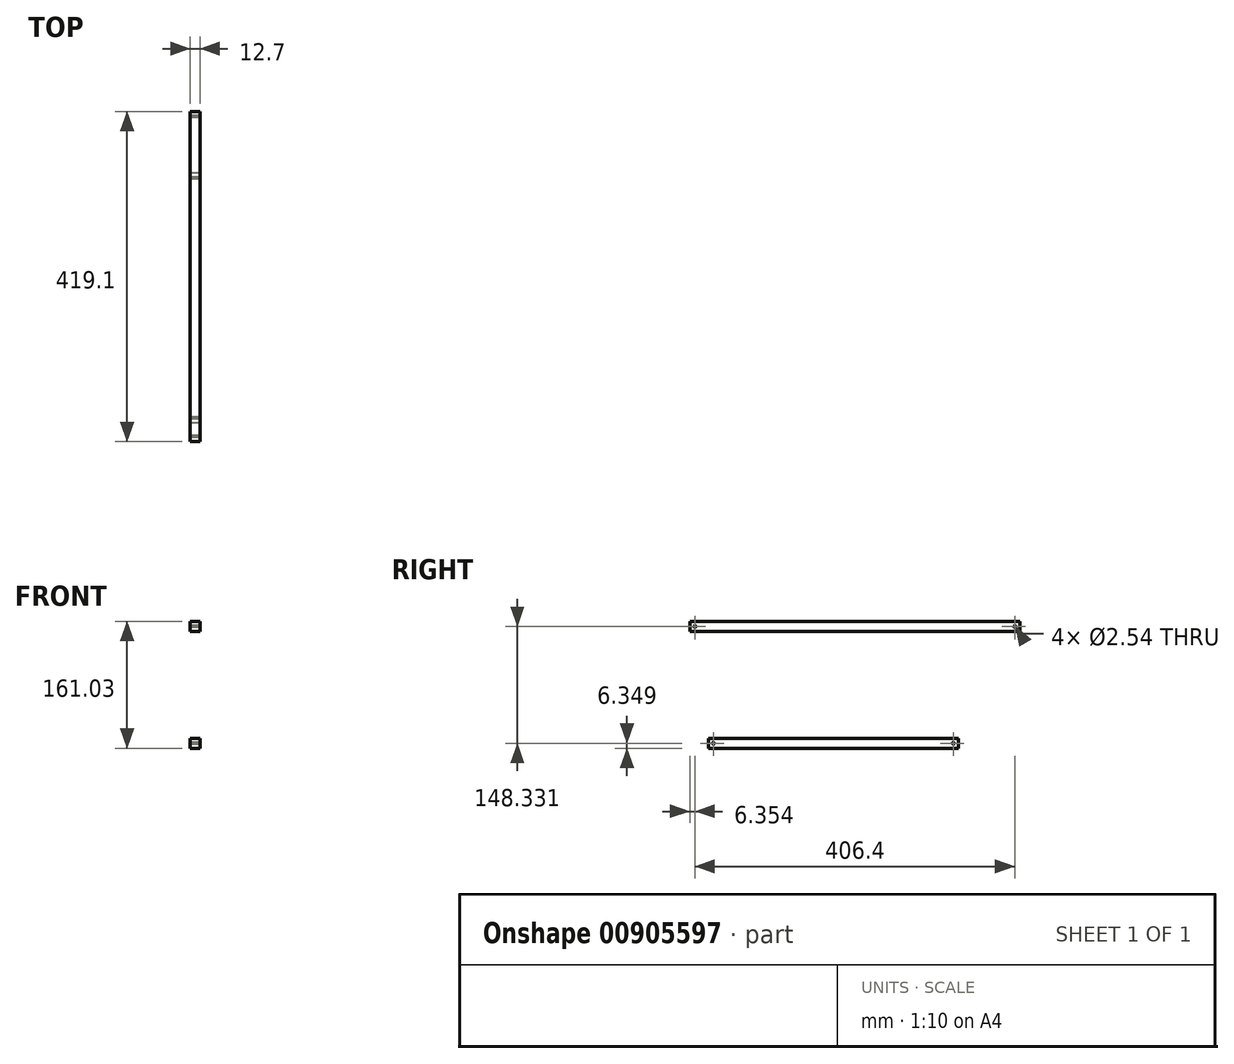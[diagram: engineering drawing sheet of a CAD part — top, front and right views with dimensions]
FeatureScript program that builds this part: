
annotation { "Feature Type Name" : "Feature", "Feature Type Description" : "" }
export const myFeature = defineFeature(function(context is Context, id is Id, definition is map)
    precondition{}
    {
        {
            var Q0;
            Q0=qCreatedBy(makeId("Right.planeOp"),FACE);
            var sketch = newSketch(context, id + "F0", { "sketchPlane" : qUnion([Q0])});
            skLineSegment(sketch, "E0", {"start": v(-773.49, 155.27) * mm, "end": v(-354.39, 155.27) * mm});
            skLineSegment(sketch, "E1", {"start": v(-773.49, 155.27) * mm, "end": v(-773.49, 142.57) * mm});
            skLineSegment(sketch, "E2", {"start": v(-773.49, 142.57) * mm, "end": v(-354.39, 142.57) * mm});
            skLineSegment(sketch, "E3", {"start": v(-354.39, 142.57) * mm, "end": v(-354.39, 155.27) * mm});
            skLineSegment(sketch, "E4", {"start": v(-750.08, 6.94) * mm, "end": v(-432.58, 6.94) * mm});
            skLineSegment(sketch, "E5", {"start": v(-432.58, 6.94) * mm, "end": v(-432.58, -5.76) * mm});
            skLineSegment(sketch, "E6", {"start": v(-432.58, -5.76) * mm, "end": v(-750.08, -5.76) * mm});
            skLineSegment(sketch, "E7", {"start": v(-750.08, -5.76) * mm, "end": v(-750.08, 6.94) * mm});
            skPoint(sketch, "E8", {"position": v(-767.14, 148.92) * mm});
            skPoint(sketch, "E9", {"position": v(-360.74, 148.92) * mm});
            skLineSegment(sketch, "E10", {"start": v(-750.08, 6.94) * mm, "end": v(-737.38, 6.94) * mm});
            skLineSegment(sketch, "E11", {"start": v(-737.38, 6.94) * mm, "end": v(-737.38, -5.76) * mm});
            skLineSegment(sketch, "E12", {"start": v(-737.38, -5.76) * mm, "end": v(-750.08, 6.94) * mm});
            skLineSegment(sketch, "E13", {"start": v(-737.38, 6.94) * mm, "end": v(-750.08, -5.76) * mm});
            skPoint(sketch, "E14", {"position": v(-743.73, 0.59) * mm});
            skLineSegment(sketch, "E15", {"start": v(-432.58, 6.94) * mm, "end": v(-445.28, 6.94) * mm});
            skLineSegment(sketch, "E16", {"start": v(-445.28, 6.94) * mm, "end": v(-445.28, -5.76) * mm});
            skLineSegment(sketch, "E17", {"start": v(-445.28, -5.76) * mm, "end": v(-432.58, 6.94) * mm});
            skLineSegment(sketch, "E18", {"start": v(-445.28, 6.94) * mm, "end": v(-432.58, -5.76) * mm});
            skPoint(sketch, "E19", {"position": v(-438.93, 0.59) * mm});
            skSolve(sketch);
        }
        {
            var Q0;
            Q0 = qSketchRegion(id + "F0", true);
            extrude(context, id + "F1", {"entities" : qUnion([Q0]), "depth" : 12.7 * mm, "offsetDistance" : 25.4 * mm});
        }
        {
            var Q0;
            Q0=sQuery(id+"F0.wireOp",VERTEX,"E9");
            var Q1;
            Q1=makeQuery(id+"F1.opExtrude","SWEPT_BODY",BODY,{"disambiguationData":[OSD([sQuery(id+"F0.wireOp",EDGE,"E0"),sQuery(id+"F0.wireOp",EDGE,"E1"),sQuery(id+"F0.wireOp",EDGE,"E2"),sQuery(id+"F0.wireOp",EDGE,"E3")])]});
            hole(context, id + "F2", {"style" : HoleStyle.SIMPLE, "endStyle" : HoleEndStyle.THROUGH, "oppositeDirection" : true, "holeDiameter" : 2.54 * mm, "majorDiameter" : 6.35 * mm, "isTappedThrough" : true, "tappedDepth" : 12.7 * mm, "tapClearance" : 3, "locations" : qUnion([Q0]), "scope" : qUnion([Q1])});
        }
        {
            var Q0;
            Q0=sQuery(id+"F0.wireOp",VERTEX,"E8");
            var Q1;
            Q1=makeQuery(id+"F1.opExtrude","SWEPT_BODY",BODY,{"disambiguationData":[OSD([sQuery(id+"F0.wireOp",EDGE,"E0"),sQuery(id+"F0.wireOp",EDGE,"E1"),sQuery(id+"F0.wireOp",EDGE,"E2"),sQuery(id+"F0.wireOp",EDGE,"E3")])]});
            hole(context, id + "F3", {"style" : HoleStyle.SIMPLE, "endStyle" : HoleEndStyle.THROUGH, "oppositeDirection" : true, "holeDiameter" : 2.54 * mm, "majorDiameter" : 6.35 * mm, "isTappedThrough" : true, "tappedDepth" : 12.7 * mm, "tapClearance" : 3, "locations" : qUnion([Q0]), "scope" : qUnion([Q1])});
        }
        {
            var Q0;
            Q0=sQuery(id+"F0.wireOp",VERTEX,"E14");
            var Q1;
            Q1=sQuery(id+"F0.wireOp",VERTEX,"E19");
            var Q2;
            Q2=makeQuery(id+"F1.opExtrude","SWEPT_BODY",BODY,{"disambiguationData":[OSD([sQuery(id+"F0.wireOp",EDGE,"E4"),sQuery(id+"F0.wireOp",EDGE,"E5"),sQuery(id+"F0.wireOp",EDGE,"E6"),sQuery(id+"F0.wireOp",EDGE,"E7"),sQuery(id+"F0.wireOp",EDGE,"E10"),sQuery(id+"F0.wireOp",EDGE,"E15")])]});
            hole(context, id + "F4", {"style" : HoleStyle.SIMPLE, "endStyle" : HoleEndStyle.THROUGH, "oppositeDirection" : true, "holeDiameter" : 2.54 * mm, "majorDiameter" : 6.35 * mm, "isTappedThrough" : true, "tappedDepth" : 12.7 * mm, "tapClearance" : 3, "locations" : qUnion([Q0, Q1]), "scope" : qUnion([Q2])});
        }
    });
